annotation { "Feature Type Name" : "Feature", "Feature Type Description" : "" }
export const myFeature = defineFeature(function(context is Context, id is Id, definition is map)
    precondition{}
    {
        {
            var Q0;
            Q0=qCreatedBy(makeId("Top.planeOp"),FACE);
            var sketch = newSketch(context, id + "F0", { "sketchPlane" : qUnion([Q0])});
            skLineSegment(sketch, "E0", {"start": v(-170.74, 60.42) * mm, "end": v(-170.74, -42.38) * mm});
            skLineSegment(sketch, "E1", {"start": v(-170.74, -42.38) * mm, "end": v(170.74, -42.38) * mm});
            skLineSegment(sketch, "E2", {"start": v(170.74, -42.38) * mm, "end": v(170.74, 59.22) * mm});
            skLineSegment(sketch, "E3", {"start": v(170.74, 59.22) * mm, "end": v(-170.74, 60.42) * mm});
            skText(sketch, "E4", { "text": "EVIL INDUSTRIES", "fontName": "OpenSans-Bold.ttf"});
            skLineSegment(sketch, "E5", {"start": v(-135.87, 0) * mm, "end": v(129.86, 0) * mm});
            skLineSegment(sketch, "E6", {"start": v(129.86, 0) * mm, "end": v(117.83, -14.73) * mm});
            skLineSegment(sketch, "E7", {"start": v(117.83, -14.73) * mm, "end": v(-126.25, -14.73) * mm});
            skLineSegment(sketch, "E8", {"start": v(-126.25, -14.73) * mm, "end": v(-135.87, 0) * mm});
            skLineSegment(sketch, "E9", {"start": v(-118.43, -26.15) * mm, "end": v(111.82, -26.15) * mm});
            skLineSegment(sketch, "E10", {"start": v(111.82, -26.15) * mm, "end": v(102.2, -37.57) * mm});
            skLineSegment(sketch, "E11", {"start": v(102.2, -37.57) * mm, "end": v(-108.21, -37.57) * mm});
            skLineSegment(sketch, "E12", {"start": v(-108.21, -37.57) * mm, "end": v(-118.43, -26.15) * mm});
            skLineSegment(sketch, "E13", {"start": v(-165.33, 53.2) * mm, "end": v(-165.64, -36.97) * mm});
            skLineSegment(sketch, "E14", {"start": v(-165.64, -36.97) * mm, "end": v(-149.1, -42.38) * mm});
            skLineSegment(sketch, "E15", {"start": v(-165.33, 53.2) * mm, "end": v(-153.3, 60.36) * mm});
            skLineSegment(sketch, "E16", {"start": v(152.1, 59.28) * mm, "end": v(164.72, 47.2) * mm});
            skLineSegment(sketch, "E17", {"start": v(164.72, 47.2) * mm, "end": v(164.72, -27.35) * mm});
            skLineSegment(sketch, "E18", {"start": v(164.72, -27.35) * mm, "end": v(156.3, -42.38) * mm});
            skLineSegment(sketch, "E19", {"start": v(-137.67, 43.59) * mm, "end": v(-125.65, 53.8) * mm});
            skLineSegment(sketch, "E20", {"start": v(-125.65, 53.8) * mm, "end": v(125.65, 53.8) * mm});
            skLineSegment(sketch, "E21", {"start": v(125.65, 53.8) * mm, "end": v(133.46, 42.38) * mm});
            skLineSegment(sketch, "E22", {"start": v(133.46, 42.38) * mm, "end": v(-137.67, 43.59) * mm});
            const initialGuessF0  = {"E4": [-0.13947, 0.01052, 1, 0, 0.02405]};
            skSetInitialGuess(sketch, initialGuessF0);
            skSolve(sketch);
        }
        {
            var Q0;
            Q0 = qSketchRegion(id + "F0", true);
            extrude(context, id + "F1", {"entities" : qUnion([Q0]), "depth" : 25.4 * mm});
        }
    });